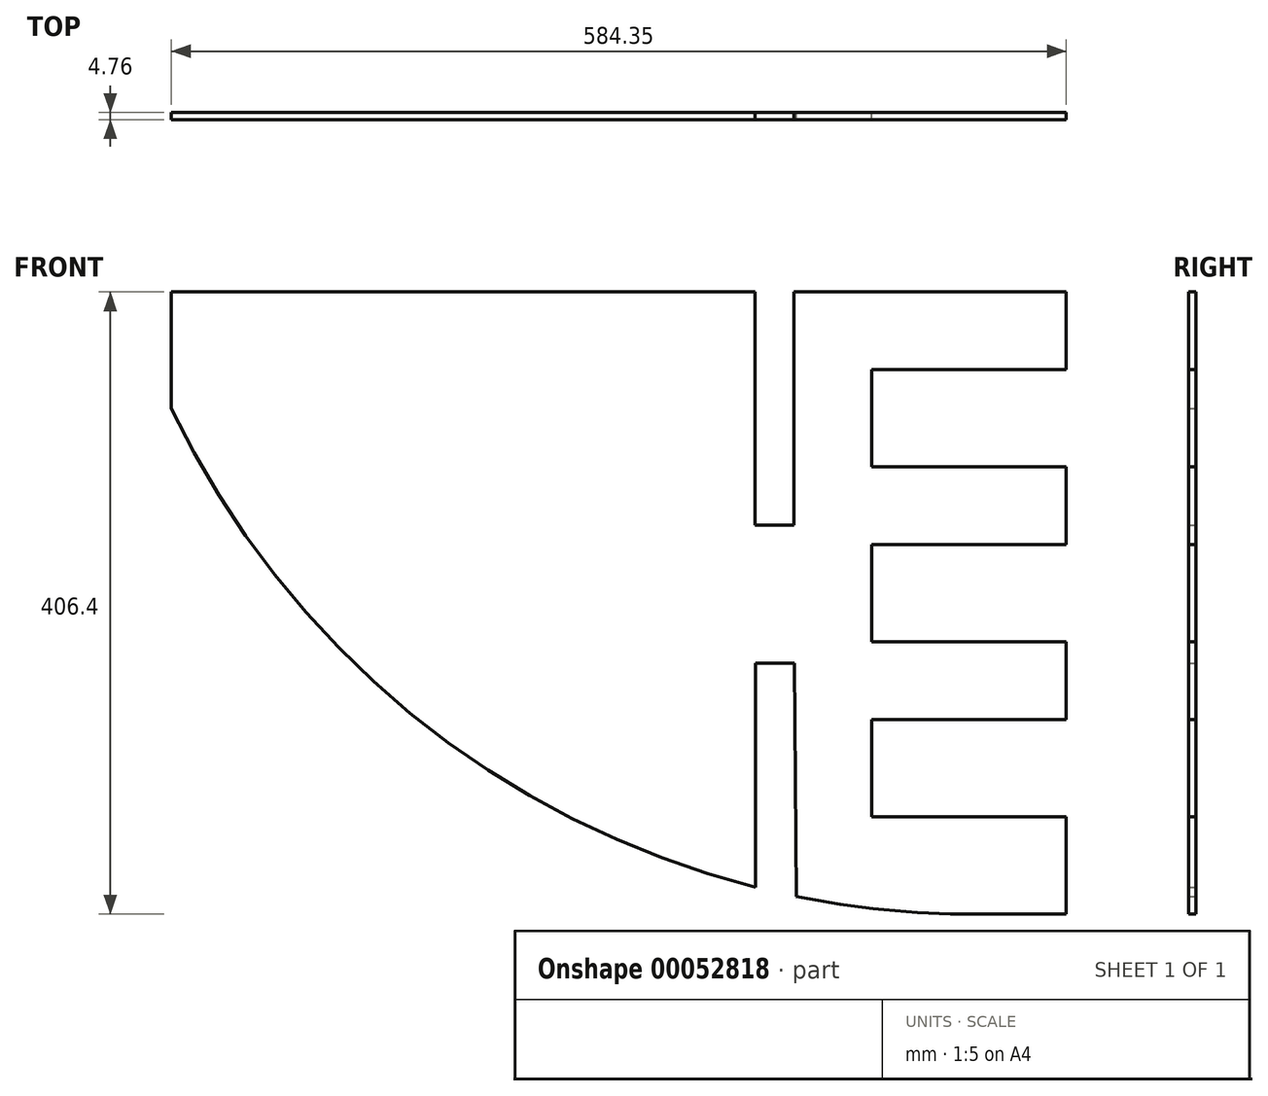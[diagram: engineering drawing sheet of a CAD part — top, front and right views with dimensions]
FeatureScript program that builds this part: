
annotation { "Feature Type Name" : "Feature", "Feature Type Description" : "" }
export const myFeature = defineFeature(function(context is Context, id is Id, definition is map)
    precondition{}
    {
        {
            var Q0;
            Q0=qCreatedBy(makeId("Front.planeOp"),FACE);
            var sketch = newSketch(context, id + "F0", { "sketchPlane" : qUnion([Q0])});
            skLineSegment(sketch, "E0", {"start": v(-584.35, 0) * mm, "end": v(-203.35, 0) * mm});
            skLineSegment(sketch, "E1", {"start": v(0, -406.4) * mm, "end": v(0, -342.9) * mm});
            skLineSegment(sketch, "E2", {"start": v(-584.35, 0) * mm, "end": v(-584.35, -76.2) * mm});
            skLineSegment(sketch, "E3", {"start": v(0, -406.4) * mm, "end": v(-60.96, -406.4) * mm});
            skArc(sketch, "E4", {"start": v(-584.35, -76.2) * mm, "mid": v(-428.47, -275.08) * mm, "end": v(-202.81, -388.78) * mm});
            skLineSegment(sketch, "E5", {"start": v(0, -50.8) * mm, "end": v(-127, -50.8) * mm});
            skLineSegment(sketch, "E6", {"start": v(-127, -50.8) * mm, "end": v(-127, -114.3) * mm});
            skLineSegment(sketch, "E7", {"start": v(-127, -114.3) * mm, "end": v(0, -114.3) * mm});
            skLineSegment(sketch, "E8", {"start": v(0, -165.1) * mm, "end": v(-127, -165.1) * mm});
            skLineSegment(sketch, "E9", {"start": v(-127, -165.1) * mm, "end": v(-127, -228.6) * mm});
            skLineSegment(sketch, "E10", {"start": v(-127, -228.6) * mm, "end": v(0, -228.6) * mm});
            skLineSegment(sketch, "E11", {"start": v(0, -279.4) * mm, "end": v(-127, -279.4) * mm});
            skLineSegment(sketch, "E12", {"start": v(-127, -279.4) * mm, "end": v(-127, -342.9) * mm});
            skLineSegment(sketch, "E13", {"start": v(-127, -342.9) * mm, "end": v(0, -342.9) * mm});
            skLineSegment(sketch, "E14.trimOffspring", {"start": v(0, -50.8) * mm, "end": v(0, 0) * mm});
            skLineSegment(sketch, "E15.trimOffspring", {"start": v(0, -165.1) * mm, "end": v(0, -114.3) * mm});
            skLineSegment(sketch, "E16.trimOffspring", {"start": v(0, -279.4) * mm, "end": v(0, -228.6) * mm});
            skLineSegment(sketch, "E17", {"start": v(-203.35, 0) * mm, "end": v(-203.35, -152.4) * mm});
            skLineSegment(sketch, "E18", {"start": v(-203.35, -152.4) * mm, "end": v(-177.95, -152.4) * mm});
            skLineSegment(sketch, "E19", {"start": v(-177.95, -152.4) * mm, "end": v(-177.95, 0) * mm});
            skLineSegment(sketch, "E20.trimOffspring", {"start": v(-177.95, 0) * mm, "end": v(0, 0) * mm});
            skLineSegment(sketch, "E21", {"start": v(-202.81, -388.78) * mm, "end": v(-202.81, -242.43) * mm});
            skLineSegment(sketch, "E22", {"start": v(-202.81, -242.43) * mm, "end": v(-177.46, -242.43) * mm});
            skLineSegment(sketch, "E23", {"start": v(-177.46, -242.43) * mm, "end": v(-176.26, -394.82) * mm});
            skArc(sketch, "E24.trimOffspring", {"start": v(-176.26, -394.82) * mm, "mid": v(-118.9, -403.5) * mm, "end": v(-60.96, -406.4) * mm});
            skSolve(sketch);
        }
        {
            var Q0;
            Q0=makeQuery(id+"F0.imprint","IMPRINT",FACE,{"disambiguationData":[TD([[makeQuery(id+"F0.imprint","IMPRINT",EDGE,{"derivedFrom":sQuery(id+"F0.wireOp",EDGE,"E0")}),-1.0]])]});
            extrude(context, id + "F1", {"entities" : qUnion([Q0]), "depth" : 4.76 * mm});
        }
    });
